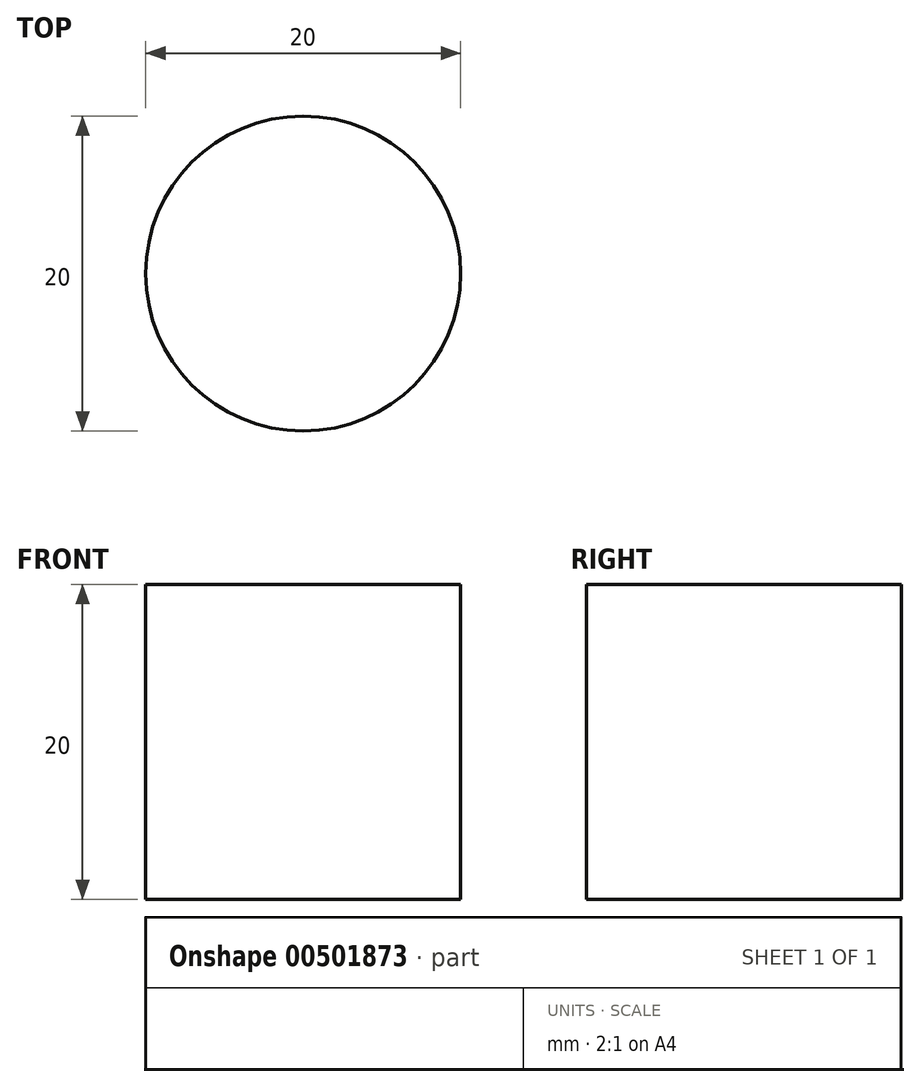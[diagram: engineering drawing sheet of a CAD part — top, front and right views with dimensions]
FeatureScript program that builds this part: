
annotation { "Feature Type Name" : "Feature", "Feature Type Description" : "" }
export const myFeature = defineFeature(function(context is Context, id is Id, definition is map)
    precondition{}
    {
        {
            var Q0;
            Q0=qCreatedBy(makeId("Top.planeOp"),FACE);
            var sketch = newSketch(context, id + "F0", { "sketchPlane" : qUnion([Q0])});
            skCircle(sketch, "E0", {"center": v(0, 0) * mm, "radius": 10 * mm});
            skSolve(sketch);
        }
        {
            var Q0;
            Q0=makeQuery(id+"F0.imprint","IMPRINT",FACE,{"disambiguationData":[TD([[makeQuery(id+"F0.imprint","IMPRINT",EDGE,{"derivedFrom":sQuery(id+"F0.wireOp",EDGE,"E0")}),1.0]])]});
            extrude(context, id + "F1", {"entities" : qUnion([Q0]), "depth" : 20 * mm});
        }
    });
